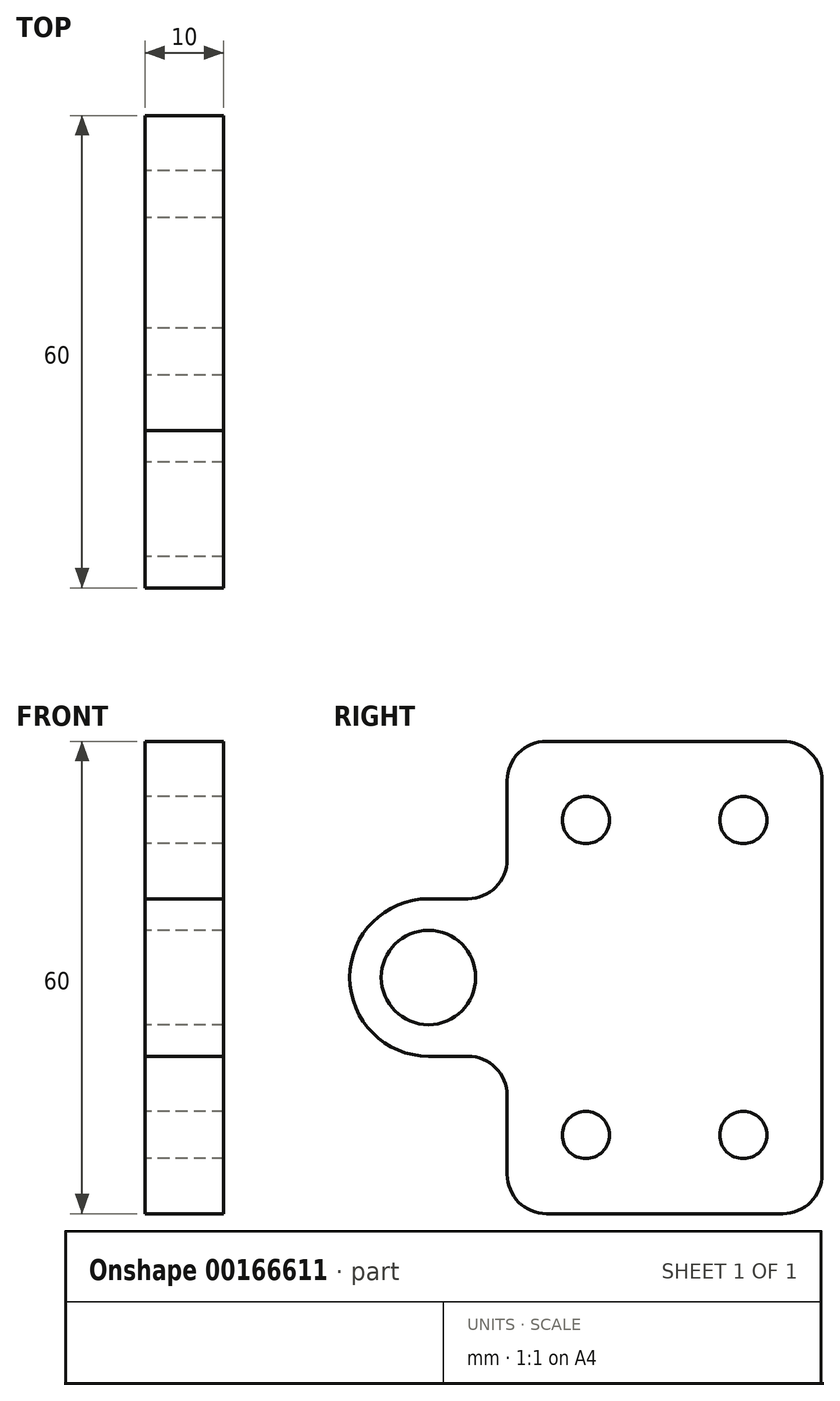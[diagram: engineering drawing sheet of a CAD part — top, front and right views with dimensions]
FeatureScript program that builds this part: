
annotation { "Feature Type Name" : "Feature", "Feature Type Description" : "" }
export const myFeature = defineFeature(function(context is Context, id is Id, definition is map)
    precondition{}
    {
        {
            var Q0;
            Q0=qCreatedBy(makeId("Right.planeOp"),FACE);
            var sketch = newSketch(context, id + "F0", { "sketchPlane" : qUnion([Q0])});
            skLineSegment(sketch, "E0.bottom", {"start": v(20, 30) * mm, "end": v(-20, 30) * mm});
            skLineSegment(sketch, "E0.top", {"start": v(20, -30) * mm, "end": v(-20, -30) * mm});
            skLineSegment(sketch, "E0.left", {"start": v(20, 30) * mm, "end": v(20, -30) * mm});
            skLineSegment(sketch, "E0.right", {"start": v(-20, 30) * mm, "end": v(-20, 10) * mm});
            skPoint(sketch, "E0.middle", {"position": v(0, 0) * mm});
            skPoint(sketch, "E1", {"position": v(-30, 0) * mm});
            skArc(sketch, "E2", {"start": v(-30, 10) * mm, "mid": v(-40, 0) * mm, "end": v(-30, -10) * mm});
            skCircle(sketch, "E3", {"center": v(-30, 0) * mm, "radius": 6 * mm});
            skLineSegment(sketch, "E4", {"start": v(-30, 10) * mm, "end": v(-20, 10) * mm});
            skLineSegment(sketch, "E5", {"start": v(-30, -10) * mm, "end": v(-20, -10) * mm});
            skLineSegment(sketch, "E6.trimOffspring", {"start": v(-20, -10) * mm, "end": v(-20, -30) * mm});
            skSolve(sketch);
        }
        {
            var Q0;
            Q0=makeQuery(id+"F0.imprint","IMPRINT",FACE,{"disambiguationData":[TD([[makeQuery(id+"F0.imprint","IMPRINT",EDGE,{"derivedFrom":sQuery(id+"F0.wireOp",EDGE,"E0.bottom")}),1.0]])]});
            extrude(context, id + "F1", {"entities" : qUnion([Q0]), "depth" : 10 * mm});
        }
        {
            var Q0;
            Q0=makeQuery(id+"F1.opExtrude","SWEPT_EDGE",EDGE,{"disambiguationData":[OSD([sQuery(id+"F0.wireOp",EDGE,"E0.bottom"),sQuery(id+"F0.wireOp",EDGE,"E0.left")])]});
            var Q1;
            Q1=makeQuery(id+"F1.opExtrude","SWEPT_EDGE",EDGE,{"disambiguationData":[OSD([sQuery(id+"F0.wireOp",EDGE,"E0.top"),sQuery(id+"F0.wireOp",EDGE,"E0.left")])]});
            var Q2;
            Q2=makeQuery(id+"F1.opExtrude","SWEPT_EDGE",EDGE,{"disambiguationData":[OSD([sQuery(id+"F0.wireOp",EDGE,"E0.bottom"),sQuery(id+"F0.wireOp",EDGE,"E0.right")])]});
            var Q3;
            Q3=makeQuery(id+"F1.opExtrude","SWEPT_EDGE",EDGE,{"disambiguationData":[OSD([sQuery(id+"F0.wireOp",EDGE,"E0.top"),sQuery(id+"F0.wireOp",EDGE,"E6.trimOffspring")])]});
            var Q4;
            Q4=makeQuery(id+"F1.opExtrude","SWEPT_EDGE",EDGE,{"disambiguationData":[OSD([sQuery(id+"F0.wireOp",EDGE,"E5"),sQuery(id+"F0.wireOp",EDGE,"E6.trimOffspring")])]});
            var Q5;
            Q5=makeQuery(id+"F1.opExtrude","SWEPT_EDGE",EDGE,{"disambiguationData":[OSD([sQuery(id+"F0.wireOp",EDGE,"E0.right"),sQuery(id+"F0.wireOp",EDGE,"E4")])]});
            fillet(context, id + "F2", {"entities" : qUnion([Q0, Q1, Q2, Q3, Q4, Q5]), "radius" : 5 * mm, "tangentPropagation" : true, "allowEdgeOverflow" : false});
        }
        {
            var Q0;
            Q0=makeQuery(id+"F1.opExtrude","CAP_FACE",FACE,{"disambiguationData":[OSD([sQuery(id+"F0.wireOp",EDGE,"E0.bottom"),sQuery(id+"F0.wireOp",EDGE,"E0.top"),sQuery(id+"F0.wireOp",EDGE,"E0.left"),sQuery(id+"F0.wireOp",EDGE,"E0.right"),sQuery(id+"F0.wireOp",EDGE,"E2"),sQuery(id+"F0.wireOp",EDGE,"E3"),sQuery(id+"F0.wireOp",EDGE,"E4"),sQuery(id+"F0.wireOp",EDGE,"E5"),sQuery(id+"F0.wireOp",EDGE,"E6.trimOffspring")])],"isStart":true});
            var sketch = newSketch(context, id + "F3", { "sketchPlane" : qUnion([Q0])});
            skPoint(sketch, "E7", {"position": v(-10, 20) * mm});
            skPoint(sketch, "E8.endSnap0", {"position": v(40, 0) * mm});
            skPoint(sketch, "E9.MirrorP", {"position": v(10, 20) * mm});
            skPoint(sketch, "E10.MirrorP", {"position": v(-10, -20) * mm});
            skPoint(sketch, "E11.MirrorP", {"position": v(10, -20) * mm});
            skSolve(sketch);
        }
        {
            var Q0;
            Q0=sQuery(id+"F3.wireOp",VERTEX,"E10.MirrorP");
            var Q1;
            Q1=sQuery(id+"F3.wireOp",VERTEX,"E11.MirrorP");
            var Q2;
            Q2=makeQuery(id+"F1.opExtrude","SWEPT_BODY",BODY,{"disambiguationData":[OSD([sQuery(id+"F0.wireOp",EDGE,"E0.bottom"),sQuery(id+"F0.wireOp",EDGE,"E0.top"),sQuery(id+"F0.wireOp",EDGE,"E0.left"),sQuery(id+"F0.wireOp",EDGE,"E0.right"),sQuery(id+"F0.wireOp",EDGE,"E2"),sQuery(id+"F0.wireOp",EDGE,"E3"),sQuery(id+"F0.wireOp",EDGE,"E4"),sQuery(id+"F0.wireOp",EDGE,"E5"),sQuery(id+"F0.wireOp",EDGE,"E6.trimOffspring")])]});
            hole(context, id + "F4", {"style" : HoleStyle.SIMPLE, "endStyle" : HoleEndStyle.THROUGH, "holeDiameter" : 6 * mm, "locations" : qUnion([Q0, Q1]), "scope" : qUnion([Q2]), "isTappedThrough" : true});
        }
        {
            var Q0;
            Q0=sQuery(id+"F3.wireOp",VERTEX,"E9.MirrorP");
            var Q1;
            Q1=sQuery(id+"F3.wireOp",VERTEX,"E7");
            var Q2;
            Q2=makeQuery(id+"F1.opExtrude","SWEPT_BODY",BODY,{"disambiguationData":[OSD([sQuery(id+"F0.wireOp",EDGE,"E0.bottom"),sQuery(id+"F0.wireOp",EDGE,"E0.top"),sQuery(id+"F0.wireOp",EDGE,"E0.left"),sQuery(id+"F0.wireOp",EDGE,"E0.right"),sQuery(id+"F0.wireOp",EDGE,"E2"),sQuery(id+"F0.wireOp",EDGE,"E3"),sQuery(id+"F0.wireOp",EDGE,"E4"),sQuery(id+"F0.wireOp",EDGE,"E5"),sQuery(id+"F0.wireOp",EDGE,"E6.trimOffspring")])]});
            hole(context, id + "F5", {"style" : HoleStyle.SIMPLE, "endStyle" : HoleEndStyle.THROUGH, "holeDiameter" : 6 * mm, "locations" : qUnion([Q0, Q1]), "scope" : qUnion([Q2]), "isTappedThrough" : true});
        }
    });
